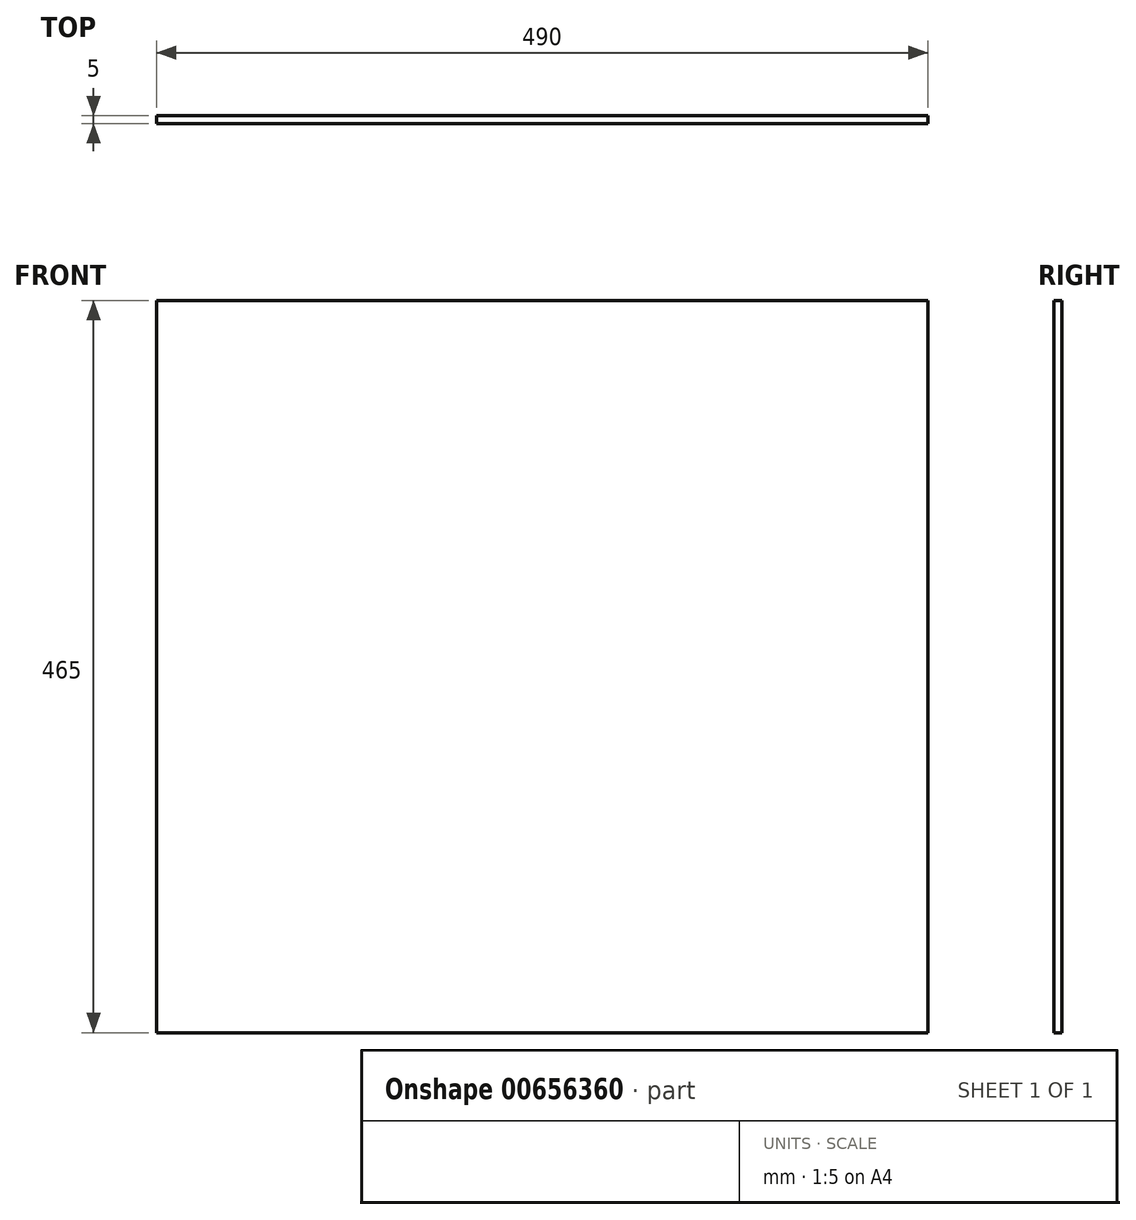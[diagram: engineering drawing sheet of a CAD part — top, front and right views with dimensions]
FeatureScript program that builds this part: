
annotation { "Feature Type Name" : "Feature", "Feature Type Description" : "" }
export const myFeature = defineFeature(function(context is Context, id is Id, definition is map)
    precondition{}
    {
        {
            var Q0;
            Q0=qCreatedBy(makeId("Top.planeOp"),FACE);
            var sketch = newSketch(context, id + "F0", { "sketchPlane" : qUnion([Q0])});
            skLineSegment(sketch, "E0.bottom", {"start": v(0, 0) * mm, "end": v(490, 0) * mm});
            skLineSegment(sketch, "E0.top", {"start": v(0, 5) * mm, "end": v(490, 5) * mm});
            skLineSegment(sketch, "E0.left", {"start": v(0, 0) * mm, "end": v(0, 5) * mm});
            skLineSegment(sketch, "E0.right", {"start": v(490, 0) * mm, "end": v(490, 5) * mm});
            skSolve(sketch);
        }
        {
            var Q0;
            Q0=makeQuery(id+"F0.imprint","IMPRINT",FACE,{"disambiguationData":[TD([[makeQuery(id+"F0.imprint","IMPRINT",EDGE,{"derivedFrom":sQuery(id+"F0.wireOp",EDGE,"E0.bottom")}),1.0]])]});
            extrude(context, id + "F1", {"entities" : qUnion([Q0]), "depth" : 465 * mm, "offsetDistance" : 25 * mm});
        }
    });
